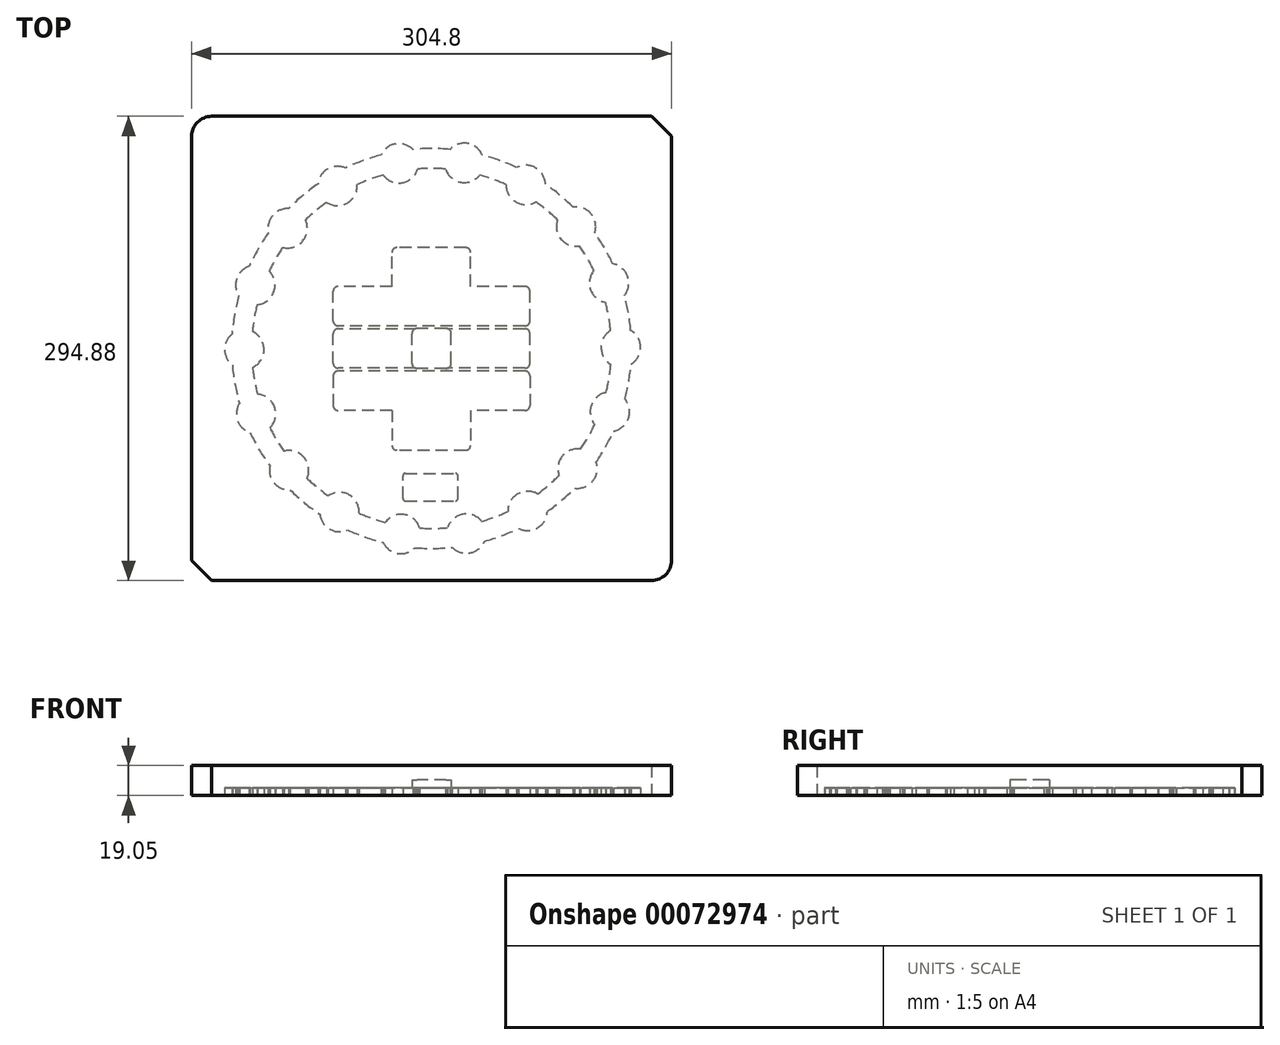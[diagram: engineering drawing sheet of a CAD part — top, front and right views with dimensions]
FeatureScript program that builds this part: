
annotation { "Feature Type Name" : "Feature", "Feature Type Description" : "" }
export const myFeature = defineFeature(function(context is Context, id is Id, definition is map)
    precondition{}
    {
        {
            var Q0;
            Q0=qCreatedBy(makeId("Top.planeOp"),FACE);
            var sketch = newSketch(context, id + "F0", { "sketchPlane" : qUnion([Q0])});
            skLineSegment(sketch, "E0.rect.bottom", {"start": v(139.7, -147.44) * mm, "end": v(-152.4, -147.44) * mm});
            skLineSegment(sketch, "E0.rect.top", {"start": v(152.4, 147.44) * mm, "end": v(-139.7, 147.44) * mm});
            skLineSegment(sketch, "E0.rect.left", {"start": v(152.4, -134.74) * mm, "end": v(152.4, 147.44) * mm});
            skLineSegment(sketch, "E0.rect.right", {"start": v(-152.4, -147.44) * mm, "end": v(-152.4, 134.74) * mm});
            skPoint(sketch, "E0.rect.middle", {"position": v(0, 0) * mm});
            skPoint(sketch, "E1.visualSharp", {"position": v(-152.4, 147.44) * mm});
            skArc(sketch, "E1.filletArc", {"start": v(-139.7, 147.44) * mm, "mid": v(-148.68, 143.72) * mm, "end": v(-152.4, 134.74) * mm});
            skPoint(sketch, "E2.visualSharp", {"position": v(152.4, -147.44) * mm});
            skArc(sketch, "E2.filletArc", {"start": v(139.7, -147.44) * mm, "mid": v(148.68, -143.72) * mm, "end": v(152.4, -134.74) * mm});
            skSolve(sketch);
        }
        {
            var Q0;
            Q0=qCreatedBy(makeId("Top.planeOp"),FACE);
            var sketch = newSketch(context, id + "F1", { "sketchPlane" : qUnion([Q0])});
            skLineSegment(sketch, "E3.rect.bottom", {"start": v(59.32, -12.5) * mm, "end": v(-59.32, -12.5) * mm});
            skLineSegment(sketch, "E3.rect.top", {"start": v(59.33, 12.5) * mm, "end": v(-59.33, 12.5) * mm});
            skLineSegment(sketch, "E3.rect.left", {"start": v(62.5, -9.32) * mm, "end": v(62.5, 9.33) * mm});
            skLineSegment(sketch, "E3.rect.right", {"start": v(-62.5, -9.33) * mm, "end": v(-62.5, 9.32) * mm});
            skPoint(sketch, "E3.rect.middle", {"position": v(0, 0) * mm});
            skPoint(sketch, "E4.visualSharp", {"position": v(-62.5, 12.5) * mm});
            skArc(sketch, "E4.filletArc", {"start": v(-59.33, 12.5) * mm, "mid": v(-61.57, 11.57) * mm, "end": v(-62.5, 9.32) * mm});
            skPoint(sketch, "E5.visualSharp", {"position": v(62.5, 12.5) * mm});
            skArc(sketch, "E5.filletArc", {"start": v(62.5, 9.33) * mm, "mid": v(61.57, 11.57) * mm, "end": v(59.33, 12.5) * mm});
            skPoint(sketch, "E6.visualSharp", {"position": v(62.5, -12.5) * mm});
            skArc(sketch, "E6.filletArc", {"start": v(59.32, -12.5) * mm, "mid": v(61.57, -11.57) * mm, "end": v(62.5, -9.32) * mm});
            skPoint(sketch, "E7.visualSharp", {"position": v(-62.5, -12.5) * mm});
            skArc(sketch, "E7.filletArc", {"start": v(-62.5, -9.33) * mm, "mid": v(-61.57, -11.57) * mm, "end": v(-59.32, -12.5) * mm});
            skPoint(sketch, "E8.0.1.0", {"position": v(-62.5, 14.37) * mm});
            skLineSegment(sketch, "E8.0.1.1", {"start": v(59.32, 14.37) * mm, "end": v(-59.32, 14.37) * mm});
            skLineSegment(sketch, "E8.0.1.2", {"start": v(59.33, 39.37) * mm, "end": v(-59.33, 39.37) * mm});
            skPoint(sketch, "E8.0.1.3", {"position": v(0, 26.87) * mm});
            skLineSegment(sketch, "E8.0.1.4", {"start": v(62.5, 17.55) * mm, "end": v(62.5, 36.2) * mm});
            skPoint(sketch, "E8.0.1.5", {"position": v(62.5, 14.37) * mm});
            skLineSegment(sketch, "E8.0.1.6", {"start": v(-62.5, 17.55) * mm, "end": v(-62.5, 36.2) * mm});
            skPoint(sketch, "E8.0.1.7", {"position": v(-62.5, 39.37) * mm});
            skPoint(sketch, "E8.0.1.8", {"position": v(62.5, 39.37) * mm});
            skArc(sketch, "E8.0.1.9", {"start": v(-62.5, 17.55) * mm, "mid": v(-61.57, 15.3) * mm, "end": v(-59.32, 14.37) * mm});
            skArc(sketch, "E8.0.1.10", {"start": v(59.32, 14.37) * mm, "mid": v(61.57, 15.3) * mm, "end": v(62.5, 17.55) * mm});
            skArc(sketch, "E8.0.1.11", {"start": v(62.5, 36.2) * mm, "mid": v(61.57, 38.44) * mm, "end": v(59.33, 39.37) * mm});
            skArc(sketch, "E8.0.1.12", {"start": v(-59.33, 39.37) * mm, "mid": v(-61.57, 38.44) * mm, "end": v(-62.5, 36.2) * mm});
            skPoint(sketch, "E8.0.2.0", {"position": v(-62.5, 41.25) * mm});
            skPoint(sketch, "E8.0.2.5", {"position": v(62.5, 41.25) * mm});
            skLineSegment(sketch, "E8.direction1", {"start": v(-62.5, -12.5) * mm, "end": v(-37.1, -12.5) * mm, "construction": true});
            skLineSegment(sketch, "E8.direction2", {"start": v(-62.5, -12.5) * mm, "end": v(-62.5, 14.37) * mm, "construction": true});
            skArc(sketch, "E9.MirrorCS", {"start": v(62.5, -36.2) * mm, "mid": v(61.57, -38.44) * mm, "end": v(59.33, -39.37) * mm});
            skArc(sketch, "E10.MirrorCS", {"start": v(-59.33, -39.37) * mm, "mid": v(-61.57, -38.44) * mm, "end": v(-62.5, -36.2) * mm});
            skArc(sketch, "E11.MirrorCS", {"start": v(59.32, -14.37) * mm, "mid": v(61.57, -15.3) * mm, "end": v(62.5, -17.55) * mm});
            skArc(sketch, "E12.MirrorCS", {"start": v(-62.5, -17.55) * mm, "mid": v(-61.57, -15.3) * mm, "end": v(-59.32, -14.37) * mm});
            skPoint(sketch, "E13.MirrorP", {"position": v(-62.5, -41.25) * mm});
            skPoint(sketch, "E14.MirrorP", {"position": v(62.5, -14.37) * mm});
            skPoint(sketch, "E15.MirrorP", {"position": v(-62.5, -39.37) * mm});
            skPoint(sketch, "E16.MirrorP", {"position": v(62.5, -41.25) * mm});
            skPoint(sketch, "E17.MirrorP", {"position": v(-62.5, -14.37) * mm});
            skLineSegment(sketch, "E18.MirrorCS", {"start": v(-62.5, -17.55) * mm, "end": v(-62.5, -36.2) * mm});
            skLineSegment(sketch, "E19.MirrorCS", {"start": v(62.5, -17.55) * mm, "end": v(62.5, -36.2) * mm});
            skLineSegment(sketch, "E20.MirrorCS", {"start": v(59.32, -14.37) * mm, "end": v(-59.32, -14.37) * mm});
            skLineSegment(sketch, "E21.MirrorCS", {"start": v(59.33, -39.37) * mm, "end": v(-59.33, -39.37) * mm});
            skPoint(sketch, "E22.MirrorP", {"position": v(62.5, -39.37) * mm});
            skPoint(sketch, "E23.MirrorP", {"position": v(0, -26.87) * mm});
            skLineSegment(sketch, "E24.rect.bottom", {"start": v(24.83, 39.08) * mm, "end": v(-25.17, 39.08) * mm});
            skLineSegment(sketch, "E24.rect.top", {"start": v(21.65, 64.08) * mm, "end": v(-22, 64.08) * mm});
            skLineSegment(sketch, "E24.rect.left", {"start": v(24.83, 39.08) * mm, "end": v(24.83, 60.9) * mm});
            skLineSegment(sketch, "E24.rect.right", {"start": v(-25.17, 39.08) * mm, "end": v(-25.17, 60.9) * mm});
            skPoint(sketch, "E24.rect.middle", {"position": v(-0.17, 51.58) * mm});
            skPoint(sketch, "E25.visualSharp", {"position": v(-25.17, 64.08) * mm});
            skArc(sketch, "E25.filletArc", {"start": v(-22, 64.08) * mm, "mid": v(-24.24, 63.15) * mm, "end": v(-25.17, 60.9) * mm});
            skPoint(sketch, "E26.visualSharp", {"position": v(24.83, 64.08) * mm});
            skArc(sketch, "E26.filletArc", {"start": v(24.83, 60.9) * mm, "mid": v(23.9, 63.15) * mm, "end": v(21.65, 64.08) * mm});
            skArc(sketch, "E27.MirrorCS", {"start": v(24.83, -61.49) * mm, "mid": v(23.9, -63.73) * mm, "end": v(21.65, -64.66) * mm});
            skArc(sketch, "E28.MirrorCS", {"start": v(-22, -64.66) * mm, "mid": v(-24.24, -63.73) * mm, "end": v(-25.17, -61.49) * mm});
            skPoint(sketch, "E29.MirrorP", {"position": v(24.83, -64.66) * mm});
            skPoint(sketch, "E30.MirrorP", {"position": v(-0.17, -52.16) * mm});
            skPoint(sketch, "E31.MirrorP", {"position": v(-25.17, -64.66) * mm});
            skLineSegment(sketch, "E32.MirrorCS", {"start": v(24.83, -38.63) * mm, "end": v(-25.17, -38.63) * mm});
            skLineSegment(sketch, "E33.MirrorCS", {"start": v(-25.17, -38.63) * mm, "end": v(-25.17, -61.49) * mm});
            skLineSegment(sketch, "E34.MirrorCS", {"start": v(21.65, -64.66) * mm, "end": v(-22, -64.66) * mm});
            skLineSegment(sketch, "E35.MirrorCS", {"start": v(24.83, -38.63) * mm, "end": v(24.83, -61.49) * mm});
            skSolve(sketch);
        }
        {
            var Q0;
            Q0=makeQuery(id+"F0.imprint","IMPRINT",FACE,{"disambiguationData":[TD([[makeQuery(id+"F0.imprint","IMPRINT",EDGE,{"derivedFrom":sQuery(id+"F0.wireOp",EDGE,"E0.rect.bottom")}),-1.0]])]});
            extrude(context, id + "F2", {"entities" : qUnion([Q0]), "depth" : 19.05 * mm});
        }
        {
            var Q0;
            Q0=makeQuery(id+"F2.opExtrude","SWEPT_EDGE",EDGE,{"disambiguationData":[OSD([sQuery(id+"F0.wireOp",EDGE,"E0.rect.bottom"),sQuery(id+"F0.wireOp",EDGE,"E0.rect.right")])]});
            var Q1;
            Q1=makeQuery(id+"F2.opExtrude","SWEPT_EDGE",EDGE,{"disambiguationData":[OSD([sQuery(id+"F0.wireOp",EDGE,"E0.rect.top"),sQuery(id+"F0.wireOp",EDGE,"E0.rect.left")])]});
            chamfer(context, id + "F3", {"entities" : qUnion([Q0, Q1]), "width" : 12.7 * mm, "tangentPropagation" : true});
        }
        {
            var Q0;
            Q0 = qSketchRegion(id + "F1", true);
            extrude(context, id + "F4", {"entities" : qUnion([Q0]), "operationType" : NewBodyOperationType.REMOVE, "depth" : 5 * mm});
        }
        {
            var Q0;
            Q0=qCreatedBy(makeId("Top.planeOp"),FACE);
            var sketch = newSketch(context, id + "F5", { "sketchPlane" : qUnion([Q0])});
            skCircle(sketch, "E36", {"center": v(-118.92, -0.69) * mm, "radius": 12.5 * mm});
            skCircle(sketch, "E37.1.0", {"center": v(-111.47, -41.54) * mm, "radius": 12.5 * mm});
            skCircle(sketch, "E37.2.0", {"center": v(-90.5, -77.38) * mm, "radius": 12.5 * mm});
            skCircle(sketch, "E37.3.0", {"center": v(-58.54, -103.89) * mm, "radius": 12.5 * mm});
            skCircle(sketch, "E37.4.0", {"center": v(-19.44, -117.86) * mm, "radius": 12.5 * mm});
            skCircle(sketch, "E37.5.0", {"center": v(22.08, -117.62) * mm, "radius": 12.5 * mm});
            skCircle(sketch, "E37.6.0", {"center": v(61.02, -103.2) * mm, "radius": 12.5 * mm});
            skCircle(sketch, "E37.7.0", {"center": v(92.67, -76.32) * mm, "radius": 12.5 * mm});
            skCircle(sketch, "E37.8.0", {"center": v(113.23, -40.25) * mm, "radius": 12.5 * mm});
            skCircle(sketch, "E37.9.0", {"center": v(120.2, 0.69) * mm, "radius": 12.5 * mm});
            skCircle(sketch, "E37.10.0", {"center": v(112.76, 41.54) * mm, "radius": 12.5 * mm});
            skCircle(sketch, "E37.11.0", {"center": v(91.79, 77.38) * mm, "radius": 12.5 * mm});
            skCircle(sketch, "E37.12.0", {"center": v(59.83, 103.89) * mm, "radius": 12.5 * mm});
            skCircle(sketch, "E37.13.0", {"center": v(20.72, 117.86) * mm, "radius": 12.5 * mm});
            skCircle(sketch, "E37.14.0", {"center": v(-20.8, 117.62) * mm, "radius": 12.5 * mm});
            skCircle(sketch, "E37.15.0", {"center": v(-59.74, 103.2) * mm, "radius": 12.5 * mm});
            skCircle(sketch, "E37.16.0", {"center": v(-91.39, 76.32) * mm, "radius": 12.5 * mm});
            skCircle(sketch, "E37.17.0", {"center": v(-111.94, 40.25) * mm, "radius": 12.5 * mm});
            skPoint(sketch, "E37.center", {"position": v(0.64, 0) * mm});
            skSolve(sketch);
        }
        {
            var Q0;
            Q0 = qSketchRegion(id + "F5", true);
            extrude(context, id + "F6", {"entities" : qUnion([Q0]), "operationType" : NewBodyOperationType.REMOVE, "depth" : 5 * mm});
        }
        {
            var Q0;
            Q0=qCreatedBy(makeId("Top.planeOp"),FACE);
            var sketch = newSketch(context, id + "F7", { "sketchPlane" : qUnion([Q0])});
            skCircle(sketch, "E38", {"center": v(0, 0) * mm, "radius": 127 * mm});
            skCircle(sketch, "E39", {"center": v(0, 0) * mm, "radius": 114.3 * mm});
            skSolve(sketch);
        }
        {
            var Q0;
            Q0=makeQuery(id+"F7.imprint","IMPRINT",FACE,{"disambiguationData":[TD([[makeQuery(id+"F7.imprint","IMPRINT",EDGE,{"derivedFrom":sQuery(id+"F7.wireOp",EDGE,"E38")}),1.0]])]});
            extrude(context, id + "F8", {"entities" : qUnion([Q0]), "operationType" : NewBodyOperationType.REMOVE, "depth" : 5 * mm});
        }
        {
            var Q0;
            Q0=qCreatedBy(makeId("Top.planeOp"),FACE);
            var sketch = newSketch(context, id + "F9", { "sketchPlane" : qUnion([Q0])});
            skLineSegment(sketch, "E40.bottom", {"start": v(-16.59, -96.84) * mm, "end": v(15.16, -96.84) * mm});
            skLineSegment(sketch, "E40.top", {"start": v(-16.59, -79.38) * mm, "end": v(15.16, -79.38) * mm});
            skLineSegment(sketch, "E40.left", {"start": v(-18.18, -95.26) * mm, "end": v(-18.18, -80.97) * mm});
            skLineSegment(sketch, "E40.right", {"start": v(16.75, -95.26) * mm, "end": v(16.75, -80.97) * mm});
            skPoint(sketch, "E41.visualSharp", {"position": v(-18.18, -96.84) * mm});
            skArc(sketch, "E41.filletArc", {"start": v(-18.18, -95.26) * mm, "mid": v(-17.71, -96.38) * mm, "end": v(-16.59, -96.84) * mm});
            skPoint(sketch, "E42.visualSharp", {"position": v(16.75, -96.84) * mm});
            skArc(sketch, "E42.filletArc", {"start": v(15.16, -96.84) * mm, "mid": v(16.28, -96.38) * mm, "end": v(16.75, -95.26) * mm});
            skPoint(sketch, "E43.visualSharp", {"position": v(16.75, -79.38) * mm});
            skArc(sketch, "E43.filletArc", {"start": v(16.75, -80.97) * mm, "mid": v(16.28, -79.85) * mm, "end": v(15.16, -79.38) * mm});
            skPoint(sketch, "E44.visualSharp", {"position": v(-18.18, -79.38) * mm});
            skArc(sketch, "E44.filletArc", {"start": v(-16.59, -79.38) * mm, "mid": v(-17.71, -79.85) * mm, "end": v(-18.18, -80.97) * mm});
            skSolve(sketch);
        }
        {
            var Q0;
            Q0=makeQuery(id+"F9.imprint","IMPRINT",FACE,{"disambiguationData":[TD([[makeQuery(id+"F9.imprint","IMPRINT",EDGE,{"derivedFrom":sQuery(id+"F9.wireOp",EDGE,"E40.bottom")}),1.0]])]});
            extrude(context, id + "F10", {"entities" : qUnion([Q0]), "operationType" : NewBodyOperationType.REMOVE, "depth" : 5 * mm});
        }
        {
            var Q0;
            Q0=qCreatedBy(makeId("Top.planeOp"),FACE);
            var sketch = newSketch(context, id + "F11", { "sketchPlane" : qUnion([Q0])});
            skLineSegment(sketch, "E45.rect.bottom", {"start": v(9.32, 12.6) * mm, "end": v(-9.32, 12.6) * mm});
            skLineSegment(sketch, "E45.rect.top", {"start": v(9.32, -12.6) * mm, "end": v(-9.32, -12.6) * mm});
            skLineSegment(sketch, "E45.rect.left", {"start": v(12.5, 9.43) * mm, "end": v(12.5, -9.43) * mm});
            skLineSegment(sketch, "E45.rect.right", {"start": v(-12.5, 9.43) * mm, "end": v(-12.5, -9.43) * mm});
            skPoint(sketch, "E45.rect.middle", {"position": v(0, 0) * mm});
            skPoint(sketch, "E46.visualSharp", {"position": v(-12.5, -12.6) * mm});
            skArc(sketch, "E46.filletArc", {"start": v(-12.5, -9.43) * mm, "mid": v(-11.57, -11.68) * mm, "end": v(-9.32, -12.6) * mm});
            skPoint(sketch, "E47.visualSharp", {"position": v(-12.5, 12.6) * mm});
            skArc(sketch, "E47.filletArc", {"start": v(-9.32, 12.6) * mm, "mid": v(-11.57, 11.68) * mm, "end": v(-12.5, 9.43) * mm});
            skPoint(sketch, "E48.visualSharp", {"position": v(12.5, 12.6) * mm});
            skArc(sketch, "E48.filletArc", {"start": v(12.5, 9.43) * mm, "mid": v(11.57, 11.68) * mm, "end": v(9.32, 12.6) * mm});
            skPoint(sketch, "E49.visualSharp", {"position": v(12.5, -12.6) * mm});
            skArc(sketch, "E49.filletArc", {"start": v(9.32, -12.6) * mm, "mid": v(11.57, -11.68) * mm, "end": v(12.5, -9.43) * mm});
            skSolve(sketch);
        }
        {
            var Q0;
            Q0=makeQuery(id+"F11.imprint","IMPRINT",FACE,{"disambiguationData":[TD([[makeQuery(id+"F11.imprint","IMPRINT",EDGE,{"derivedFrom":sQuery(id+"F11.wireOp",EDGE,"E45.rect.bottom")}),1.0]])]});
            extrude(context, id + "F12", {"entities" : qUnion([Q0]), "operationType" : NewBodyOperationType.REMOVE, "depth" : 10 * mm});
        }
    });
